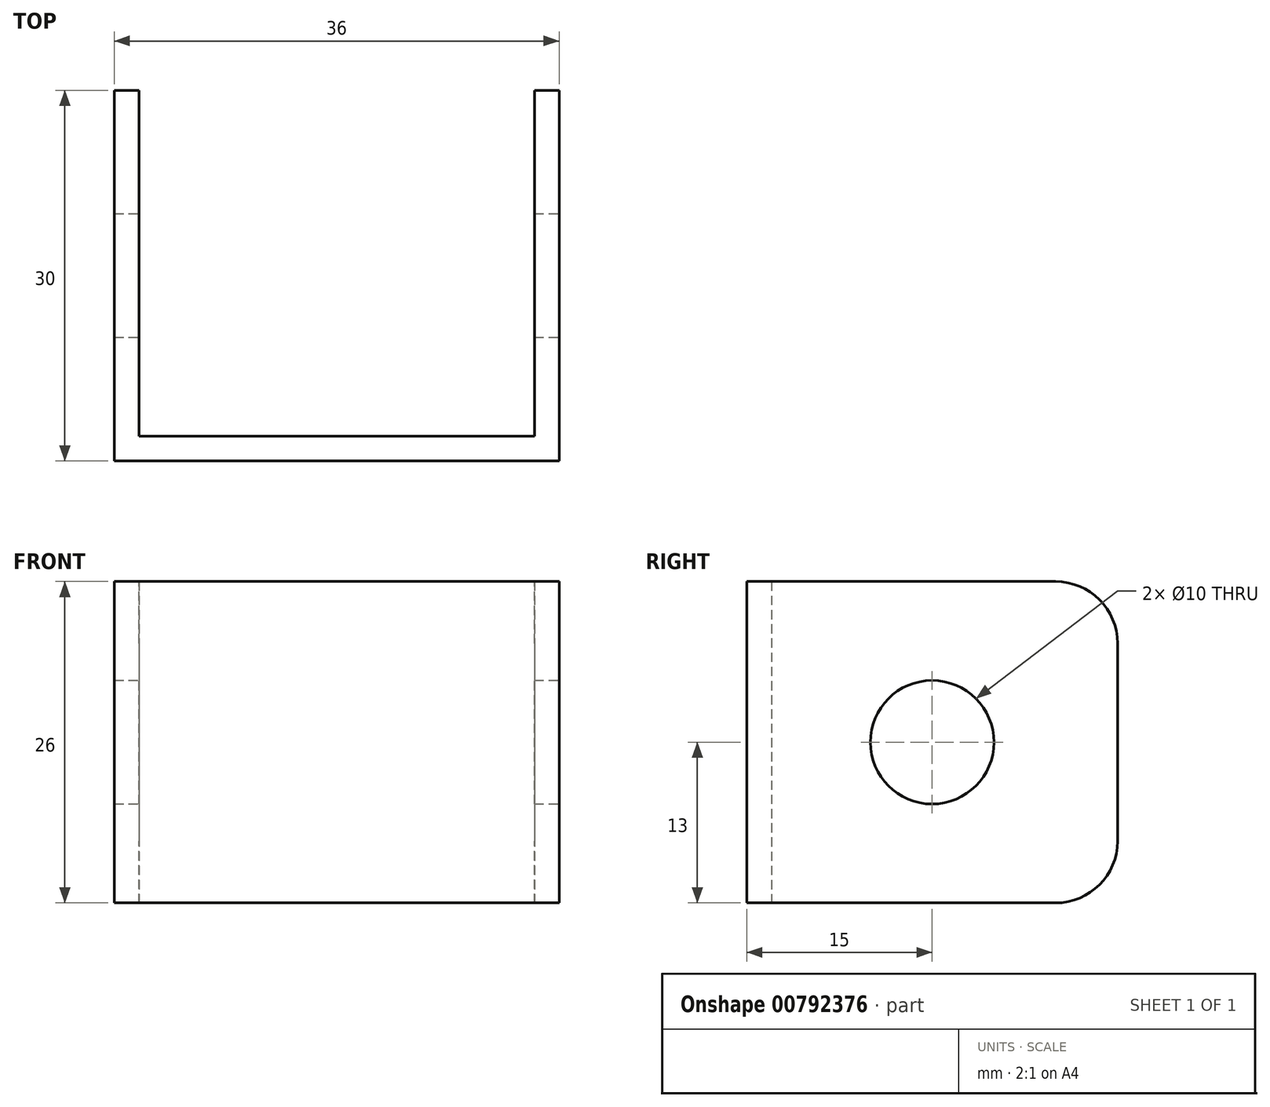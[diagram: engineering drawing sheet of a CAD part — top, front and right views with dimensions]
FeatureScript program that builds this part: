
annotation { "Feature Type Name" : "Feature", "Feature Type Description" : "" }
export const myFeature = defineFeature(function(context is Context, id is Id, definition is map)
    precondition{}
    {
        {
            var Q0;
            Q0=qCreatedBy(makeId("Top.planeOp"),FACE);
            var sketch = newSketch(context, id + "F0", { "sketchPlane" : qUnion([Q0])});
            skLineSegment(sketch, "E0.bottom", {"start": v(-18, 15) * mm, "end": v(-16, 15) * mm});
            skLineSegment(sketch, "E0.top", {"start": v(-18, -15) * mm, "end": v(18, -15) * mm});
            skLineSegment(sketch, "E0.left", {"start": v(-18, 15) * mm, "end": v(-18, -15) * mm});
            skLineSegment(sketch, "E0.right", {"start": v(18, 15) * mm, "end": v(18, -15) * mm});
            skPoint(sketch, "E0.middle", {"position": v(0, 0) * mm});
            skLineSegment(sketch, "E1.0", {"start": v(16, 15) * mm, "end": v(16, -13) * mm});
            skLineSegment(sketch, "E2.0", {"start": v(-16, 15) * mm, "end": v(-16, -13) * mm});
            skLineSegment(sketch, "E3.0", {"start": v(-16, -13) * mm, "end": v(16, -13) * mm});
            skLineSegment(sketch, "E4.trimOffspring", {"start": v(16, 15) * mm, "end": v(18, 15) * mm});
            skSolve(sketch);
        }
        {
            var Q0;
            Q0 = qSketchRegion(id + "F0", true);
            extrude(context, id + "F1", {"entities" : qUnion([Q0]), "depth" : 26 * mm, "offsetDistance" : 25 * mm});
        }
        {
            var Q0;
            Q0=makeQuery(id+"F1.opExtrude","SWEPT_FACE",FACE,{"disambiguationData":[OSD([sQuery(id+"F0.wireOp",EDGE,"E0.right")])]});
            var sketch = newSketch(context, id + "F2", { "sketchPlane" : qUnion([Q0])});
            skCircle(sketch, "E5", {"center": v(0, 13) * mm, "radius": 5 * mm});
            skPoint(sketch, "E5.centerSnap0", {"position": v(15, 13) * mm});
            skSolve(sketch);
        }
        {
            var Q0;
            Q0 = qSketchRegion(id + "F2", true);
            extrude(context, id + "F3", {"entities" : qUnion([Q0]), "operationType" : NewBodyOperationType.REMOVE, "endBound" : BoundingType.THROUGH_ALL, "oppositeDirection" : true, "depth" : 25 * mm, "offsetDistance" : 25 * mm});
        }
        {
            var Q0;
            Q0=makeQuery(id+"F1.opExtrude","CAP_EDGE",EDGE,{"disambiguationData":[OSD([sQuery(id+"F0.wireOp",EDGE,"E4.trimOffspring")])],"isStart":true});
            var Q1;
            Q1=makeQuery(id+"F1.opExtrude","CAP_EDGE",EDGE,{"disambiguationData":[OSD([sQuery(id+"F0.wireOp",EDGE,"E0.bottom")])],"isStart":true});
            var Q2;
            Q2=makeQuery(id+"F1.opExtrude","CAP_EDGE",EDGE,{"disambiguationData":[OSD([sQuery(id+"F0.wireOp",EDGE,"E0.bottom")])],"isStart":false});
            var Q3;
            Q3=makeQuery(id+"F1.opExtrude","CAP_EDGE",EDGE,{"disambiguationData":[OSD([sQuery(id+"F0.wireOp",EDGE,"E4.trimOffspring")])],"isStart":false});
            fillet(context, id + "F4", {"entities" : qUnion([Q0, Q1, Q2, Q3]), "radius" : 5 * mm, "tangentPropagation" : true, "allowEdgeOverflow" : false});
        }
    });
